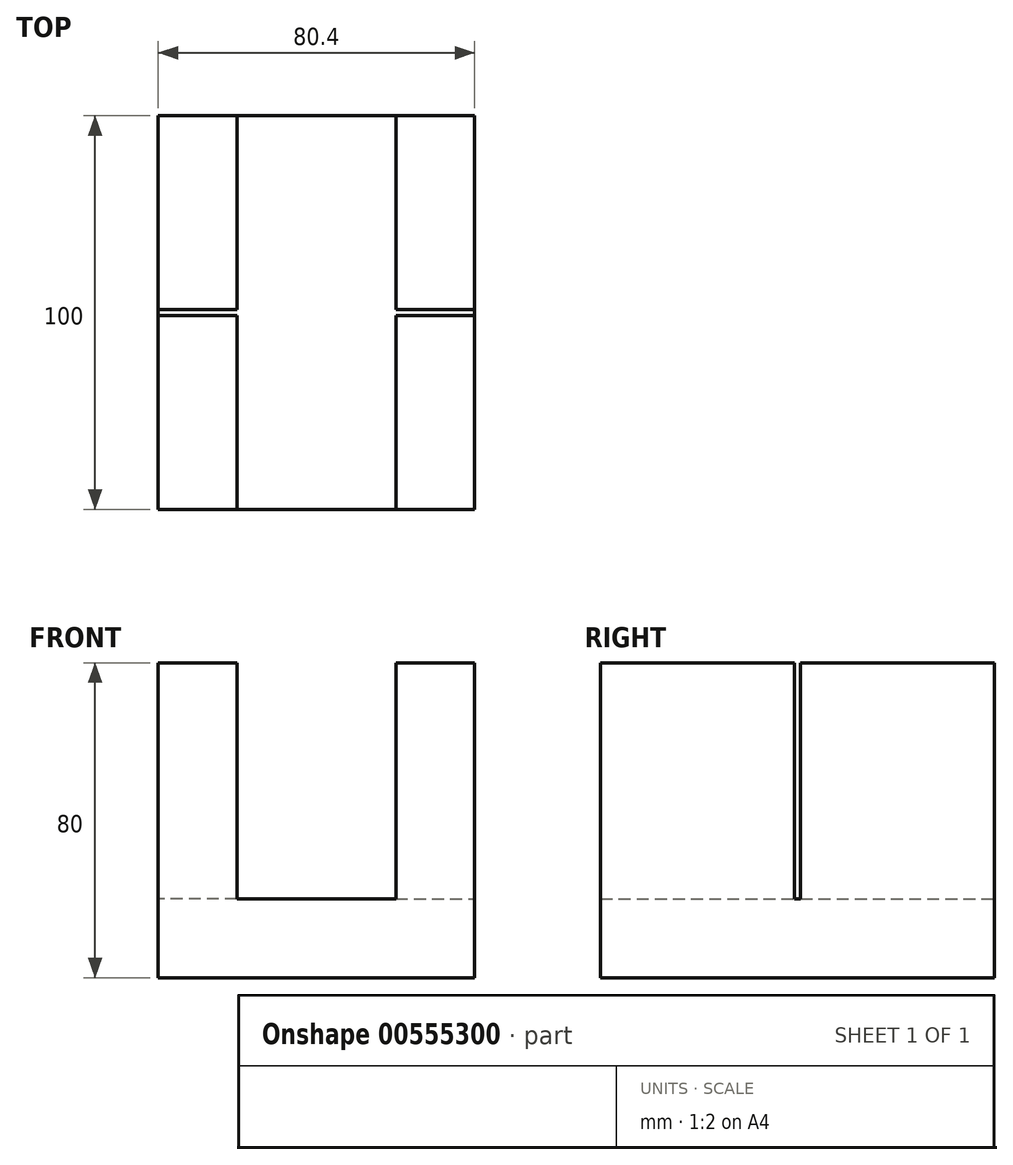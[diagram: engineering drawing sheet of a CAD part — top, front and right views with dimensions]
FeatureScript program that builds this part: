
annotation { "Feature Type Name" : "Feature", "Feature Type Description" : "" }
export const myFeature = defineFeature(function(context is Context, id is Id, definition is map)
    precondition{}
    {
        {
            var Q0;
            Q0=qCreatedBy(makeId("Front.planeOp"),FACE);
            var sketch = newSketch(context, id + "F0", { "sketchPlane" : qUnion([Q0])});
            skLineSegment(sketch, "E0.bottom", {"start": v(20.2, 20) * mm, "end": v(-20.2, 20) * mm});
            skLineSegment(sketch, "E0.top", {"start": v(20.2, -20) * mm, "end": v(-20.2, -20) * mm});
            skLineSegment(sketch, "E0.left", {"start": v(20.2, 20) * mm, "end": v(20.2, -20) * mm});
            skLineSegment(sketch, "E0.right", {"start": v(-20.2, 20) * mm, "end": v(-20.2, -20) * mm});
            skPoint(sketch, "E0.middle", {"position": v(0, 0) * mm});
            skLineSegment(sketch, "E1.bottom", {"start": v(40.2, -40) * mm, "end": v(-40.2, -40) * mm});
            skLineSegment(sketch, "E1.top", {"start": v(40.2, 40) * mm, "end": v(-40.2, 40) * mm});
            skLineSegment(sketch, "E1.left", {"start": v(40.2, -40) * mm, "end": v(40.2, 40) * mm});
            skLineSegment(sketch, "E1.right", {"start": v(-40.2, -40) * mm, "end": v(-40.2, 40) * mm});
            skLineSegment(sketch, "E2.bottom", {"start": v(-20.2, 20) * mm, "end": v(20.2, 20) * mm});
            skLineSegment(sketch, "E2.top", {"start": v(-20.2, 40) * mm, "end": v(20.2, 40) * mm});
            skLineSegment(sketch, "E2.left", {"start": v(-20.2, 20) * mm, "end": v(-20.2, 40) * mm});
            skLineSegment(sketch, "E2.right", {"start": v(20.2, 20) * mm, "end": v(20.2, 40) * mm});
            skLineSegment(sketch, "E3", {"start": v(-20.2, -20) * mm, "end": v(-40.2, -20) * mm});
            skLineSegment(sketch, "E4", {"start": v(-40.2, -20) * mm, "end": v(20.2, -20) * mm});
            skLineSegment(sketch, "E5", {"start": v(20.2, -20) * mm, "end": v(40.2, -20) * mm});
            skSolve(sketch);
        }
        {
            var Q0;
            {var subQ6=sQuery(id+"F0.wireOp",EDGE,"E0.right");Q0=makeQuery(id+"F0.imprint","IMPRINT",FACE,{"disambiguationData":[TD([[makeQuery(id+"F0.imprint","IMPRINT",EDGE,{"derivedFrom":subQ6}),-1.0]])]});}
            var Q1;
            {var subQ4=sQuery(id+"F0.wireOp",EDGE,"E1.bottom");Q1=makeQuery(id+"F0.imprint","IMPRINT",FACE,{"disambiguationData":[TD([[makeQuery(id+"F0.imprint","IMPRINT",EDGE,{"derivedFrom":subQ4}),-1.0]])]});}
            var Q2;
            Q2=makeQuery(id+"F0.imprint","IMPRINT",FACE,{"disambiguationData":[TD([[makeQuery(id+"F0.imprint","IMPRINT",EDGE,{"derivedFrom":sQuery(id+"F0.wireOp",EDGE,"E0.left")}),1.0]])]});
            extrude(context, id + "F1", {"entities" : qUnion([Q0, Q1, Q2]), "depth" : 100 * mm, "offsetDistance" : 25 * mm, "symmetric" : true});
        }
        {
            var Q0;
            {var subQ6=sQuery(id+"F0.wireOp",EDGE,"E0.right");Q0=makeQuery(id+"F0.imprint","IMPRINT",FACE,{"disambiguationData":[TD([[makeQuery(id+"F0.imprint","IMPRINT",EDGE,{"derivedFrom":subQ6}),-1.0]])]});}
            var Q1;
            Q1=makeQuery(id+"F0.imprint","IMPRINT",FACE,{"disambiguationData":[TD([[makeQuery(id+"F0.imprint","IMPRINT",EDGE,{"derivedFrom":sQuery(id+"F0.wireOp",EDGE,"E0.left")}),1.0]])]});
            extrude(context, id + "F2", {"entities" : qUnion([Q0, Q1]), "operationType" : NewBodyOperationType.REMOVE, "depth" : 1.6 * mm, "offsetDistance" : 25 * mm, "symmetric" : true});
        }
    });
